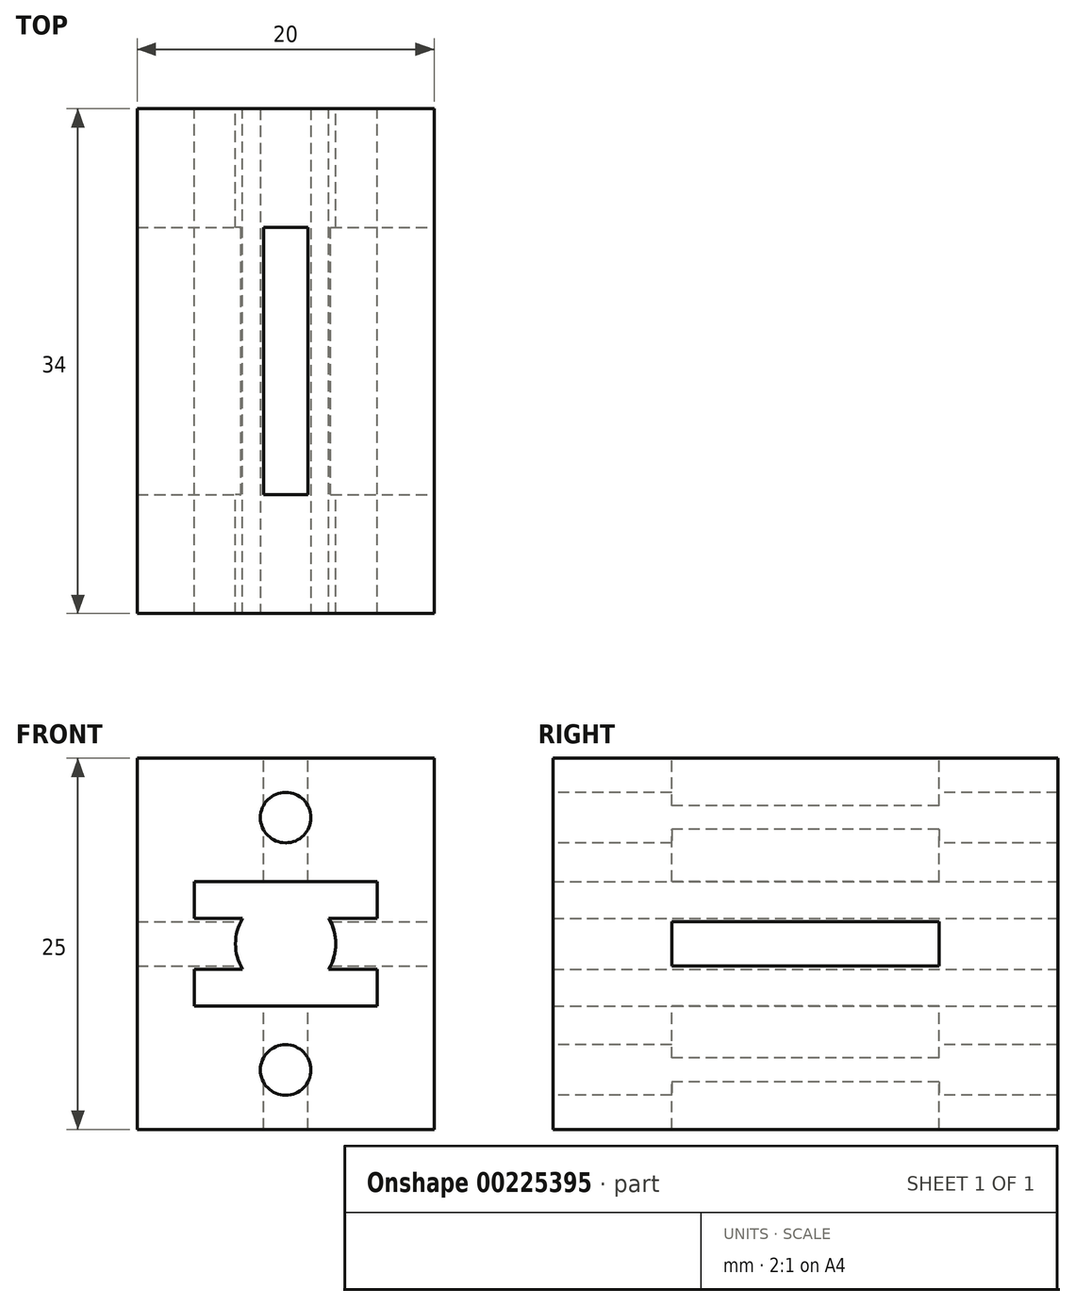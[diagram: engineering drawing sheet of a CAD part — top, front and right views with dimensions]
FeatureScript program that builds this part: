
annotation { "Feature Type Name" : "Feature", "Feature Type Description" : "" }
export const myFeature = defineFeature(function(context is Context, id is Id, definition is map)
    precondition{}
    {
        {
            var Q0;
            Q0=qCreatedBy(makeId("Front.planeOp"),FACE);
            var sketch = newSketch(context, id + "F0", { "sketchPlane" : qUnion([Q0])});
            skLineSegment(sketch, "E0.bottom", {"start": v(-5, 12.5) * mm, "end": v(5, 12.5) * mm, "construction": true});
            skLineSegment(sketch, "E0.top", {"start": v(-5, -12.5) * mm, "end": v(5, -12.5) * mm, "construction": true});
            skLineSegment(sketch, "E0.left", {"start": v(-5, 12.5) * mm, "end": v(-5, -12.5) * mm, "construction": true});
            skLineSegment(sketch, "E0.right", {"start": v(5, 12.5) * mm, "end": v(5, -12.5) * mm, "construction": true});
            skPoint(sketch, "E0.middle", {"position": v(0, 0) * mm});
            skCircle(sketch, "E1", {"center": v(5, 0) * mm, "radius": 3.17 * mm, "construction": true});
            skCircle(sketch, "E2", {"center": v(2.05, 2.95) * mm, "radius": 1 * mm, "construction": true});
            skCircle(sketch, "E3", {"center": v(2.05, -2.95) * mm, "radius": 1 * mm, "construction": true});
            skLineSegment(sketch, "E4", {"start": v(5, 0) * mm, "end": v(2.05, 2.95) * mm, "construction": true});
            skLineSegment(sketch, "E5", {"start": v(2.05, -2.95) * mm, "end": v(5, 0) * mm, "construction": true});
            skLineSegment(sketch, "E6.bottom", {"start": v(-1.15, 4.2) * mm, "end": v(3.25, 4.2) * mm, "construction": true});
            skLineSegment(sketch, "E6.top", {"start": v(-1.15, 1.7) * mm, "end": v(3.25, 1.7) * mm, "construction": true});
            skLineSegment(sketch, "E6.left", {"start": v(-1.15, 4.2) * mm, "end": v(-1.15, 1.7) * mm, "construction": true});
            skLineSegment(sketch, "E6.right", {"start": v(3.25, 4.2) * mm, "end": v(3.25, 1.7) * mm, "construction": true});
            skPoint(sketch, "E6.middle", {"position": v(1.05, 2.95) * mm});
            skLineSegment(sketch, "E7.MirrorCS", {"start": v(-1.15, -1.7) * mm, "end": v(3.25, -1.7) * mm, "construction": true});
            skLineSegment(sketch, "E8.MirrorCS", {"start": v(-1.15, -4.2) * mm, "end": v(-1.15, -1.7) * mm, "construction": true});
            skLineSegment(sketch, "E9.MirrorCS", {"start": v(-1.15, -4.2) * mm, "end": v(3.25, -4.2) * mm, "construction": true});
            skLineSegment(sketch, "E10.MirrorCS", {"start": v(3.25, -4.2) * mm, "end": v(3.25, -1.7) * mm, "construction": true});
            skLineSegment(sketch, "E11", {"start": v(-1.15, 4.2) * mm, "end": v(5, 4.2) * mm});
            skLineSegment(sketch, "E12", {"start": v(5, 12.5) * mm, "end": v(5, 4.2) * mm});
            skLineSegment(sketch, "E13", {"start": v(5, 12.5) * mm, "end": v(-5, 12.5) * mm});
            skLineSegment(sketch, "E14", {"start": v(-5, 12.5) * mm, "end": v(-5, -12.5) * mm});
            skLineSegment(sketch, "E15", {"start": v(-5, -12.5) * mm, "end": v(5, -12.5) * mm});
            skArc(sketch, "E16", {"start": v(2.09, 1.7) * mm, "mid": v(1.62, 0) * mm, "end": v(2.09, -1.7) * mm});
            skLineSegment(sketch, "E17", {"start": v(-1.15, 4.2) * mm, "end": v(-1.15, 1.7) * mm});
            skLineSegment(sketch, "E18", {"start": v(-1.15, 1.7) * mm, "end": v(2.09, 1.7) * mm});
            skLineSegment(sketch, "E19", {"start": v(-1.15, -1.7) * mm, "end": v(2.09, -1.7) * mm});
            skLineSegment(sketch, "E20", {"start": v(-1.15, -1.7) * mm, "end": v(-1.15, -4.2) * mm});
            skLineSegment(sketch, "E21", {"start": v(-1.15, -4.2) * mm, "end": v(5, -4.2) * mm});
            skLineSegment(sketch, "E22", {"start": v(5, -4.2) * mm, "end": v(5, -12.5) * mm});
            skCircle(sketch, "E23", {"center": v(0.05, 2.95) * mm, "radius": 1 * mm, "construction": true});
            skLineSegment(sketch, "E24", {"start": v(5, 0) * mm, "end": v(5, 15.82) * mm, "construction": true});
            skLineSegment(sketch, "E25", {"start": v(5, 15.82) * mm, "end": v(5, -17.9) * mm, "construction": true});
            skLineSegment(sketch, "E26.MirrorCS", {"start": v(11.15, 1.7) * mm, "end": v(7.91, 1.7) * mm});
            skLineSegment(sketch, "E27.MirrorCS", {"start": v(15, -12.5) * mm, "end": v(5, -12.5) * mm});
            skLineSegment(sketch, "E28.MirrorCS", {"start": v(5, 12.5) * mm, "end": v(15, 12.5) * mm});
            skLineSegment(sketch, "E29.MirrorCS", {"start": v(11.15, 4.2) * mm, "end": v(11.15, 1.7) * mm});
            skLineSegment(sketch, "E30.MirrorCS", {"start": v(15, 12.5) * mm, "end": v(15, -12.5) * mm});
            skLineSegment(sketch, "E31.MirrorCS", {"start": v(11.15, -1.7) * mm, "end": v(11.15, -4.2) * mm});
            skLineSegment(sketch, "E32.MirrorCS", {"start": v(11.15, -1.7) * mm, "end": v(7.91, -1.7) * mm});
            skLineSegment(sketch, "E33.MirrorCS", {"start": v(15, -12.5) * mm, "end": v(5, -12.5) * mm, "construction": true});
            skLineSegment(sketch, "E34.MirrorCS", {"start": v(11.15, -4.2) * mm, "end": v(6.75, -4.2) * mm, "construction": true});
            skLineSegment(sketch, "E35.MirrorCS", {"start": v(11.15, 4.2) * mm, "end": v(11.15, 1.7) * mm, "construction": true});
            skLineSegment(sketch, "E36.MirrorCS", {"start": v(6.75, -4.2) * mm, "end": v(6.75, -1.7) * mm, "construction": true});
            skLineSegment(sketch, "E37.MirrorCS", {"start": v(11.15, 4.2) * mm, "end": v(5, 4.2) * mm});
            skPoint(sketch, "E38.MirrorP", {"position": v(10, 0) * mm});
            skCircle(sketch, "E39.MirrorC", {"center": v(9.95, 2.95) * mm, "radius": 1 * mm, "construction": true});
            skLineSegment(sketch, "E40.MirrorCS", {"start": v(15, 12.5) * mm, "end": v(15, -12.5) * mm, "construction": true});
            skCircle(sketch, "E41.MirrorC", {"center": v(7.95, 2.95) * mm, "radius": 1 * mm, "construction": true});
            skLineSegment(sketch, "E42.MirrorCS", {"start": v(11.15, 1.7) * mm, "end": v(6.75, 1.7) * mm, "construction": true});
            skLineSegment(sketch, "E43.MirrorCS", {"start": v(11.15, -4.2) * mm, "end": v(11.15, -1.7) * mm, "construction": true});
            skCircle(sketch, "E44.MirrorC", {"center": v(7.95, -2.95) * mm, "radius": 1 * mm, "construction": true});
            skLineSegment(sketch, "E45.MirrorCS", {"start": v(11.15, -1.7) * mm, "end": v(6.75, -1.7) * mm, "construction": true});
            skArc(sketch, "E46.MirrorCS", {"start": v(7.91, 1.7) * mm, "mid": v(8.37, 0) * mm, "end": v(7.91, -1.7) * mm});
            skLineSegment(sketch, "E47.MirrorCS", {"start": v(6.75, 4.2) * mm, "end": v(6.75, 1.7) * mm, "construction": true});
            skLineSegment(sketch, "E48.MirrorCS", {"start": v(7.95, -2.95) * mm, "end": v(5, 0) * mm, "construction": true});
            skLineSegment(sketch, "E49.MirrorCS", {"start": v(11.15, -4.2) * mm, "end": v(5, -4.2) * mm});
            skPoint(sketch, "E50.MirrorP", {"position": v(8.95, 2.95) * mm});
            skLineSegment(sketch, "E51.MirrorCS", {"start": v(5, 0) * mm, "end": v(7.95, 2.95) * mm, "construction": true});
            skLineSegment(sketch, "E52.MirrorCS", {"start": v(15, 12.5) * mm, "end": v(5, 12.5) * mm, "construction": true});
            skLineSegment(sketch, "E53.MirrorCS", {"start": v(11.15, 4.2) * mm, "end": v(6.75, 4.2) * mm, "construction": true});
            skSolve(sketch);
        }
        {
            var Q0;
            Q0=makeQuery(id+"F0.imprint","IMPRINT",FACE,{"disambiguationData":[TD([[makeQuery(id+"F0.imprint","IMPRINT",EDGE,{"derivedFrom":sQuery(id+"F0.wireOp",EDGE,"E11")}),1.0]])]});
            var Q1;
            Q1=makeQuery(id+"F0.imprint","IMPRINT",FACE,{"disambiguationData":[TD([[makeQuery(id+"F0.imprint","IMPRINT",EDGE,{"derivedFrom":sQuery(id+"F0.wireOp",EDGE,"E26.MirrorCS")}),1.0]])]});
            extrude(context, id + "F1", {"entities" : qUnion([Q0, Q1]), "endBound" : BoundingType.SYMMETRIC, "offsetDistance" : 25 * mm, "depth" : 34 * mm});
        }
        {
            var Q0;
            Q0=makeQuery(id+"F1.opExtrude","SWEPT_FACE",FACE,{"disambiguationData":[OSD([sQuery(id+"F0.wireOp",EDGE,"E13"),sQuery(id+"F0.wireOp",EDGE,"E28.MirrorCS")])]});
            var sketch = newSketch(context, id + "F2", { "sketchPlane" : qUnion([Q0])});
            skPoint(sketch, "E54.0", {"position": v(5, 17) * mm});
            skPoint(sketch, "E55.0", {"position": v(5, -17) * mm});
            skPoint(sketch, "E56.0", {"position": v(15, 0) * mm});
            skPoint(sketch, "E57.0", {"position": v(-5, 0) * mm});
            skLineSegment(sketch, "E58.bottom", {"start": v(3.5, 9) * mm, "end": v(6.5, 9) * mm});
            skLineSegment(sketch, "E58.top", {"start": v(3.5, -9) * mm, "end": v(6.5, -9) * mm});
            skLineSegment(sketch, "E58.left", {"start": v(3.5, 9) * mm, "end": v(3.5, -9) * mm});
            skLineSegment(sketch, "E58.right", {"start": v(6.5, 9) * mm, "end": v(6.5, -9) * mm});
            skPoint(sketch, "E58.middle", {"position": v(5, 0) * mm});
            skSolve(sketch);
        }
        {
            var Q0;
            Q0=makeQuery(id+"F2.imprint","IMPRINT",FACE,{"disambiguationData":[TD([[makeQuery(id+"F2.imprint","IMPRINT",EDGE,{"derivedFrom":sQuery(id+"F2.wireOp",EDGE,"E58.bottom")}),-1.0]])]});
            extrude(context, id + "F3", {"entities" : qUnion([Q0]), "operationType" : NewBodyOperationType.REMOVE, "endBound" : BoundingType.THROUGH_ALL, "oppositeDirection" : true, "depth" : 25 * mm, "offsetDistance" : 25 * mm});
        }
        {
            var Q0;
            Q0=makeQuery(id+"F1.opExtrude","SWEPT_FACE",FACE,{"disambiguationData":[OSD([sQuery(id+"F0.wireOp",EDGE,"E30.MirrorCS")])]});
            var sketch = newSketch(context, id + "F4", { "sketchPlane" : qUnion([Q0])});
            skLineSegment(sketch, "E59.bottom", {"start": v(-9, -1.5) * mm, "end": v(9, -1.5) * mm});
            skLineSegment(sketch, "E59.top", {"start": v(-9, 1.5) * mm, "end": v(9, 1.5) * mm});
            skLineSegment(sketch, "E59.left", {"start": v(-9, -1.5) * mm, "end": v(-9, 1.5) * mm});
            skLineSegment(sketch, "E59.right", {"start": v(9, -1.5) * mm, "end": v(9, 1.5) * mm});
            skPoint(sketch, "E59.middle", {"position": v(0, 0) * mm});
            skSolve(sketch);
        }
        {
            var Q0;
            Q0=makeQuery(id+"F4.imprint","IMPRINT",FACE,{"disambiguationData":[TD([[makeQuery(id+"F4.imprint","IMPRINT",EDGE,{"derivedFrom":sQuery(id+"F4.wireOp",EDGE,"E59.bottom")}),1.0]])]});
            extrude(context, id + "F5", {"entities" : qUnion([Q0]), "operationType" : NewBodyOperationType.REMOVE, "endBound" : BoundingType.THROUGH_ALL, "oppositeDirection" : true, "depth" : 25 * mm, "offsetDistance" : 25 * mm});
        }
        {
            var Q0;
            Q0=makeQuery(id+"F1.opExtrude","CAP_FACE",FACE,{"disambiguationData":[OSD([sQuery(id+"F0.wireOp",EDGE,"E11"),sQuery(id+"F0.wireOp",EDGE,"E13"),sQuery(id+"F0.wireOp",EDGE,"E14"),sQuery(id+"F0.wireOp",EDGE,"E15"),sQuery(id+"F0.wireOp",EDGE,"E16"),sQuery(id+"F0.wireOp",EDGE,"E17"),sQuery(id+"F0.wireOp",EDGE,"E18"),sQuery(id+"F0.wireOp",EDGE,"E19"),sQuery(id+"F0.wireOp",EDGE,"E20"),sQuery(id+"F0.wireOp",EDGE,"E21"),sQuery(id+"F0.wireOp",EDGE,"E26.MirrorCS"),sQuery(id+"F0.wireOp",EDGE,"E27.MirrorCS"),sQuery(id+"F0.wireOp",EDGE,"E28.MirrorCS"),sQuery(id+"F0.wireOp",EDGE,"E29.MirrorCS"),sQuery(id+"F0.wireOp",EDGE,"E30.MirrorCS"),sQuery(id+"F0.wireOp",EDGE,"E31.MirrorCS"),sQuery(id+"F0.wireOp",EDGE,"E32.MirrorCS"),sQuery(id+"F0.wireOp",EDGE,"E37.MirrorCS"),sQuery(id+"F0.wireOp",EDGE,"E46.MirrorCS"),sQuery(id+"F0.wireOp",EDGE,"E49.MirrorCS")])],"isStart":false});
            var sketch = newSketch(context, id + "F6", { "sketchPlane" : qUnion([Q0])});
            skPoint(sketch, "E60", {"position": v(5, 8.5) * mm});
            skPoint(sketch, "E60.positionSnap0", {"position": v(5, 4.2) * mm});
            skPoint(sketch, "E61", {"position": v(5, -8.5) * mm});
            skSolve(sketch);
        }
        {
            var Q0;
            Q0=sQuery(id+"F6.wireOp",VERTEX,"E60");
            var Q1;
            Q1=sQuery(id+"F6.wireOp",VERTEX,"E61");
            var Q2;
            Q2=makeQuery(id+"F1.opExtrude","SWEPT_BODY",BODY,{"disambiguationData":[OSD([sQuery(id+"F0.wireOp",EDGE,"E11"),sQuery(id+"F0.wireOp",EDGE,"E13"),sQuery(id+"F0.wireOp",EDGE,"E14"),sQuery(id+"F0.wireOp",EDGE,"E15"),sQuery(id+"F0.wireOp",EDGE,"E16"),sQuery(id+"F0.wireOp",EDGE,"E17"),sQuery(id+"F0.wireOp",EDGE,"E18"),sQuery(id+"F0.wireOp",EDGE,"E19"),sQuery(id+"F0.wireOp",EDGE,"E20"),sQuery(id+"F0.wireOp",EDGE,"E21"),sQuery(id+"F0.wireOp",EDGE,"E26.MirrorCS"),sQuery(id+"F0.wireOp",EDGE,"E27.MirrorCS"),sQuery(id+"F0.wireOp",EDGE,"E28.MirrorCS"),sQuery(id+"F0.wireOp",EDGE,"E29.MirrorCS"),sQuery(id+"F0.wireOp",EDGE,"E30.MirrorCS"),sQuery(id+"F0.wireOp",EDGE,"E31.MirrorCS"),sQuery(id+"F0.wireOp",EDGE,"E32.MirrorCS"),sQuery(id+"F0.wireOp",EDGE,"E37.MirrorCS"),sQuery(id+"F0.wireOp",EDGE,"E46.MirrorCS"),sQuery(id+"F0.wireOp",EDGE,"E49.MirrorCS")])]});
            hole(context, id + "F7", {"style" : HoleStyle.SIMPLE, "endStyle" : HoleEndStyle.BLIND, "standardTappedOrClearance" : lookupTablePath({ "fit" : "Normal", "standard" : "ISO", "size" : "M3", "type" : "Clearance" }), "standardBlindInLast" : lookupTablePath({ "fit" : "Normal", "standard" : "ISO", "engagement" : "75%", "pitch" : "0.5 mm", "size" : "M3", "type" : "Clearance & tapped" }), "holeDiameter" : 3.4 * mm, "majorDiameter" : 5 * mm, "holeDepth" : 35 * mm, "isTappedThrough" : true, "tappedDepth" : 12 * mm, "tapClearance" : 3, "startFromSketch" : true, "locations" : qUnion([Q0, Q1]), "scope" : qUnion([Q2])});
        }
    });
